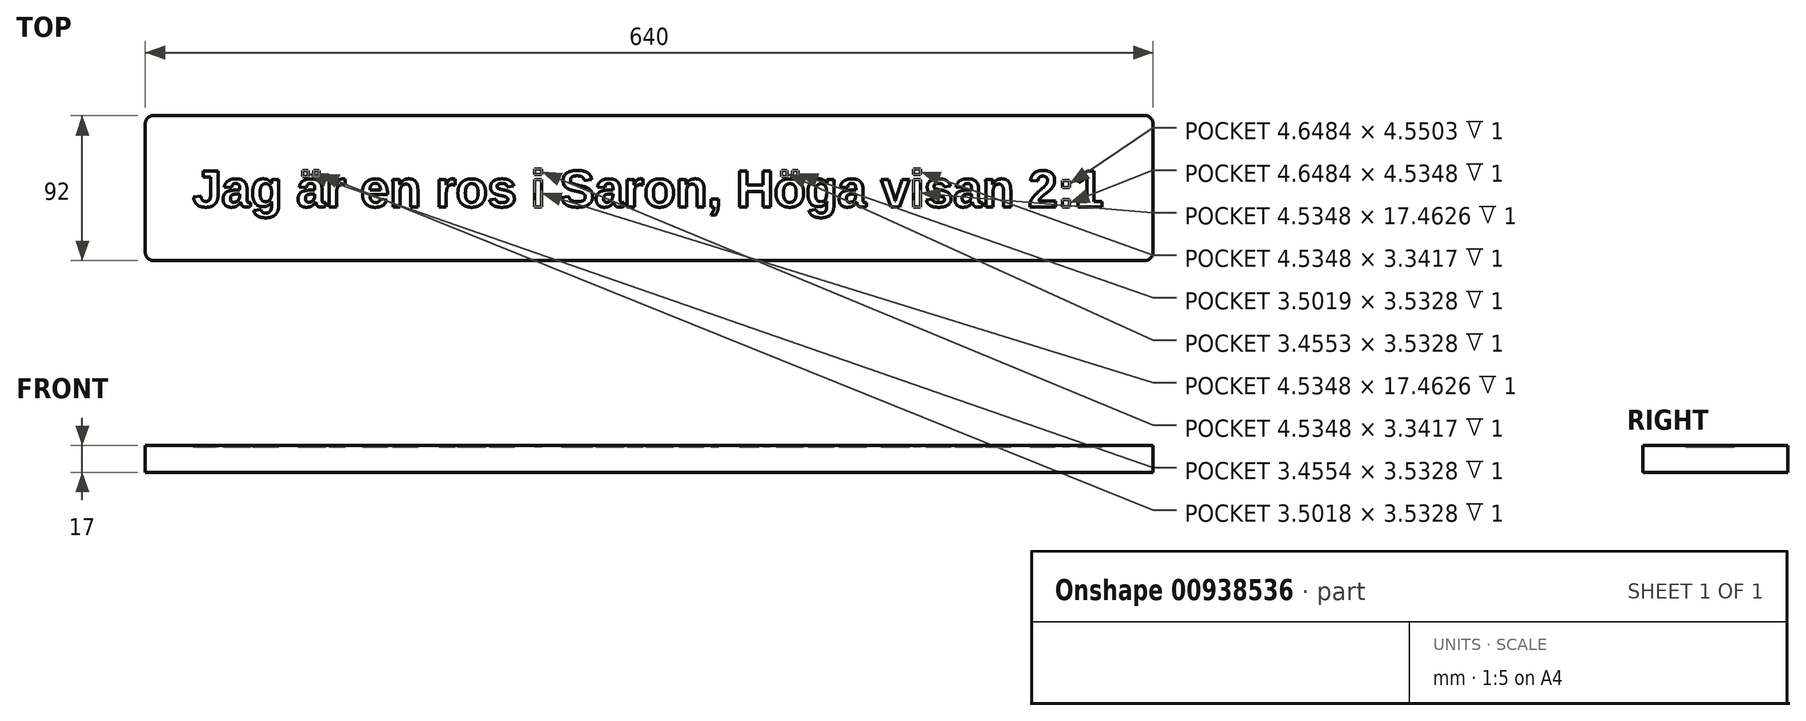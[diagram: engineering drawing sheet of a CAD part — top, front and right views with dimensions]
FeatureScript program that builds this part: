
annotation { "Feature Type Name" : "Feature", "Feature Type Description" : "" }
export const myFeature = defineFeature(function(context is Context, id is Id, definition is map)
    precondition{}
    {
        {
            var Q0;
            Q0=qCreatedBy(makeId("Top.planeOp"),FACE);
            var sketch = newSketch(context, id + "F0", { "sketchPlane" : qUnion([Q0])});
            skLineSegment(sketch, "E0.bottom", {"start": v(-627.84, 74.97) * mm, "end": v(2.16, 74.97) * mm});
            skLineSegment(sketch, "E0.top", {"start": v(-627.84, -17.03) * mm, "end": v(2.16, -17.03) * mm});
            skLineSegment(sketch, "E0.left", {"start": v(-632.84, 69.97) * mm, "end": v(-632.84, -12.03) * mm});
            skLineSegment(sketch, "E0.right", {"start": v(7.16, 69.97) * mm, "end": v(7.16, -12.03) * mm});
            skPoint(sketch, "E1.visualSharp", {"position": v(-632.84, 74.97) * mm});
            skArc(sketch, "E1.filletArc", {"start": v(-627.84, 74.97) * mm, "mid": v(-631.37, 73.51) * mm, "end": v(-632.84, 69.97) * mm});
            skPoint(sketch, "E2.visualSharp", {"position": v(-632.84, -17.03) * mm});
            skArc(sketch, "E2.filletArc", {"start": v(-632.84, -12.03) * mm, "mid": v(-631.37, -15.56) * mm, "end": v(-627.84, -17.03) * mm});
            skPoint(sketch, "E3.visualSharp", {"position": v(7.16, 74.97) * mm});
            skArc(sketch, "E3.filletArc", {"start": v(7.16, 69.97) * mm, "mid": v(5.7, 73.51) * mm, "end": v(2.16, 74.97) * mm});
            skPoint(sketch, "E4.visualSharp", {"position": v(7.16, -17.03) * mm});
            skArc(sketch, "E4.filletArc", {"start": v(2.16, -17.03) * mm, "mid": v(5.7, -15.56) * mm, "end": v(7.16, -12.03) * mm});
            skSolve(sketch);
        }
        {
            var Q0;
            Q0=qSketchRegion(id+"F0",true);
            extrude(context, id + "F1", {"entities" : qUnion([Q0]), "depth" : 17 * mm, "offsetDistance" : 25 * mm});
        }
        {
            var Q0;
            Q0=makeQuery(id+"F1.opExtrude","CAP_FACE",FACE,{"disambiguationData":[OSD([sQuery(id+"F0.wireOp",EDGE,"E0.bottom"),sQuery(id+"F0.wireOp",EDGE,"E0.top"),sQuery(id+"F0.wireOp",EDGE,"E0.left"),sQuery(id+"F0.wireOp",EDGE,"E0.right")])],"isStart":false});
            var sketch = newSketch(context, id + "F2", { "sketchPlane" : qUnion([Q0])});
            skPoint(sketch, "E5.firstSnap0", {"position": v(-131.57, 11.72) * mm});
            skText(sketch, "E6", { "text": "Jag är en ros i Saron, Höga visan 2:1", "fontName": "Arimo-Bold.ttf"});
            skLineSegment(sketch, "E7", {"start": v(-312.84, 74.97) * mm, "end": v(-312.84, -17.03) * mm, "construction": true});
            skPoint(sketch, "E8.startSnap0", {"position": v(-22.84, 28.97) * mm});
            skPoint(sketch, "E8.endSnap0", {"position": v(-632.84, 28.97) * mm});
            skLineSegment(sketch, "E9", {"start": v(-632.84, 28.97) * mm, "end": v(7.16, 28.97) * mm, "construction": true});
            const initialGuessF2  = {"E6": [-0.60284, 0.01708, 1, 0, 0.0238]};
            skSetInitialGuess(sketch, initialGuessF2);
            skSolve(sketch);
        }
        {
            var Q0;
            Q0=qSketchRegion(id+"F2",true);
            extrude(context, id + "F3", {"entities" : qUnion([Q0]), "operationType" : NewBodyOperationType.REMOVE, "oppositeDirection" : true, "depth" : 1 * mm, "offsetDistance" : 25 * mm});
        }
    });
